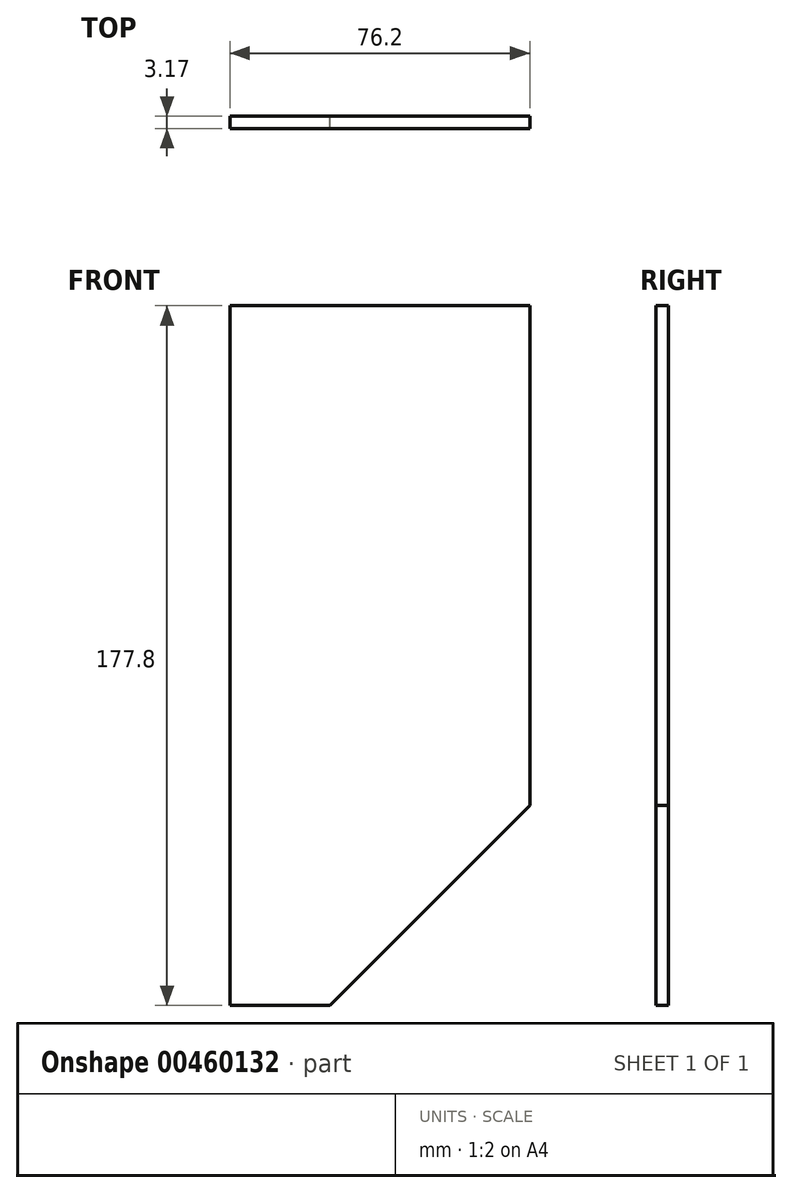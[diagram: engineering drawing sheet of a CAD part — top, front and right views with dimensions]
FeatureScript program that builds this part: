
annotation { "Feature Type Name" : "Feature", "Feature Type Description" : "" }
export const myFeature = defineFeature(function(context is Context, id is Id, definition is map)
    precondition{}
    {
        {
            var Q0;
            Q0=qCreatedBy(makeId("Front.planeOp"),FACE);
            var sketch = newSketch(context, id + "F0", { "sketchPlane" : qUnion([Q0])});
            skLineSegment(sketch, "E0", {"start": v(0, 0) * mm, "end": v(0, 177.8) * mm});
            skLineSegment(sketch, "E1", {"start": v(0, 177.8) * mm, "end": v(76.2, 177.8) * mm});
            skLineSegment(sketch, "E2", {"start": v(76.2, 177.8) * mm, "end": v(76.2, 50.8) * mm});
            skLineSegment(sketch, "E3", {"start": v(76.2, 50.8) * mm, "end": v(25.4, 0) * mm});
            skLineSegment(sketch, "E4", {"start": v(25.4, 0) * mm, "end": v(0, 0) * mm});
            skLineSegment(sketch, "E5", {"start": v(25.4, 0) * mm, "end": v(89.47, 0) * mm, "construction": true});
            skSolve(sketch);
        }
        {
            var Q0;
            Q0=makeQuery(id+"F0.imprint","IMPRINT",FACE,{"disambiguationData":[TD([[makeQuery(id+"F0.imprint","IMPRINT",EDGE,{"derivedFrom":sQuery(id+"F0.wireOp",EDGE,"E0")}),-1.0]])]});
            extrude(context, id + "F1", {"entities" : qUnion([Q0]), "depth" : 3.17 * mm});
        }
    });
